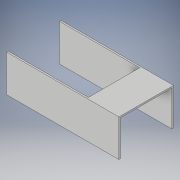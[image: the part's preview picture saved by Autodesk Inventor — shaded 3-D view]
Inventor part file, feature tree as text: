
AUTODESK INVENTOR PART (.ipt)
format: ipt  version: 2017 (Build 210142000, 142)  size: 133,632 bytes
history: native  units: in
note: dims shown in document units (in); Inventor stores cm internally (conversion verified against a paired STEP export)
features: extrude x6, sketch x6
ambient origin geometry x8: Origin, YZ Plane, XZ Plane, XY Plane, X Axis, Y Axis, Z Axis, Center Point
bodies: Solid1 (feature_tree)
feature tree (12):
  extrude  "Extrusion1"  Depth=5.75in
  extrude  "Extrusion2"  Depth=5.0in
  extrude  "Extrusion3"  Depth=8.0in TaperAngle=0.0deg
  extrude  "Extrusion4"  Depth=5.5in TaperAngle=0.0deg
  extrude  "Extrusion5"  Depth=13.75in TaperAngle=0.0deg
  extrude  "Extrusion6"  [1 undecoded]
  sketch  "Sketch1"  dims[d0=3.75in d1=5.75in]
  sketch  "Sketch2"  dims[d2=0.25in d3=0.0in d4=5.0in]
  sketch  "Sketch3"  dims[d5=0.25in d6=8.0in d7=0.0in]
  sketch  "Sketch4"  dims[d8=0.25in d9=0.0in d10=5.5in d11=0.0in]
  sketch  "Sketch5"  dims[d12=13.75in d13=0.0in d14=13.75in d15=0.0in]
  sketch  "Sketch6"
note: 1 required parameter value undecoded (feature->parameter linkage not recoverable at this tier; creation-order binding heuristic only, values carry confidence <= 0.55)
